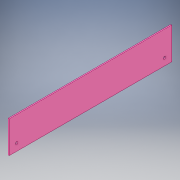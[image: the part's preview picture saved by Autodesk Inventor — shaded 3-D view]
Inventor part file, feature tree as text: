
AUTODESK INVENTOR PART (.ipt)
format: ipt  version: 2017 (Build 210142000, 142)  size: 107,520 bytes
history: native  units: in
note: dims shown in document units (in); Inventor stores cm internally (conversion verified against a paired STEP export)
features: extrude x3, sketch x3
ambient origin geometry x8: Origin, YZ Plane, XZ Plane, XY Plane, X Axis, Y Axis, Z Axis, Center Point
bodies: Solid1 (feature_tree)
feature tree (6):
  extrude  "Extrusion1"  Depth=3.875in
  extrude  "Extrusion2"  Depth=0.125in
  extrude  "Extrusion3"  Depth=0.125in
  sketch  "Sketch1"  dims[d0=19.75in d1=3.875in]
  sketch  "Sketch2"  dims[d2=0.125in d3=0.0in d4=0.875in]
  sketch  "Sketch3"  dims[d5=0.875in d6=0.3125in d7=0.125in d8=0.0in d11=0.875in d12=0.875in d13=0.3125in d14=0.125in d15=0.0in]
